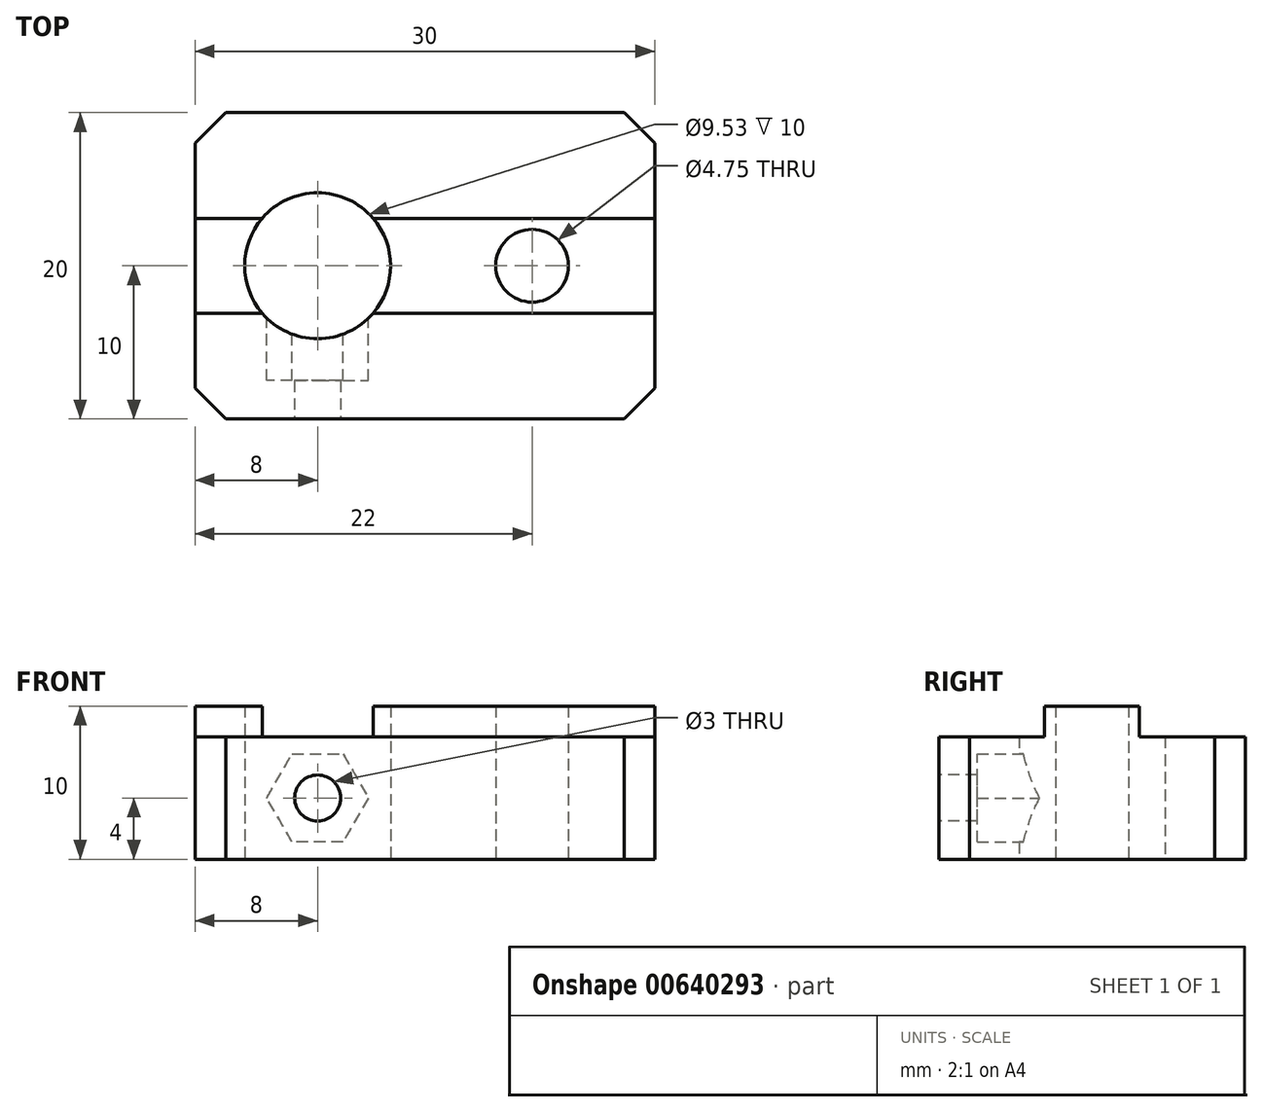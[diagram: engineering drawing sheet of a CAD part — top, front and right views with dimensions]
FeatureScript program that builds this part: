
annotation { "Feature Type Name" : "Feature", "Feature Type Description" : "" }
export const myFeature = defineFeature(function(context is Context, id is Id, definition is map)
    precondition{}
    {
        {
            var Q0;
            Q0=qCreatedBy(makeId("Top.planeOp"),FACE);
            var sketch = newSketch(context, id + "F0", { "sketchPlane" : qUnion([Q0])});
            skCircle(sketch, "E0", {"center": v(0, 0) * mm, "radius": 4.76 * mm});
            skLineSegment(sketch, "E1", {"start": v(0, 0) * mm, "end": v(0, 10) * mm, "construction": true});
            skLineSegment(sketch, "E2", {"start": v(0, 10) * mm, "end": v(-8, 10) * mm});
            skLineSegment(sketch, "E3", {"start": v(-8, 10) * mm, "end": v(-8, -10) * mm});
            skLineSegment(sketch, "E4", {"start": v(-8, -10) * mm, "end": v(22, -10) * mm});
            skLineSegment(sketch, "E5", {"start": v(22, -10) * mm, "end": v(22, 10) * mm});
            skLineSegment(sketch, "E6", {"start": v(22, 10) * mm, "end": v(0, 10) * mm});
            skLineSegment(sketch, "E7", {"start": v(22, 0) * mm, "end": v(14, 0) * mm, "construction": true});
            skPoint(sketch, "E7.endSnap0", {"position": v(22, 0) * mm});
            skCircle(sketch, "E8", {"center": v(14, 0) * mm, "radius": 2.38 * mm});
            skCircle(sketch, "E9", {"center": v(14, 0) * mm, "radius": 4.58 * mm, "construction": true});
            skSolve(sketch);
        }
        {
            var Q0;
            Q0 = qSketchRegion(id + "F0", true);
            extrude(context, id + "F1", {"entities" : qUnion([Q0]), "depth" : 8 * mm, "offsetDistance" : 25 * mm});
        }
        {
            var Q0;
            Q0=makeQuery(id+"F1.opExtrude","CAP_FACE",FACE,{"disambiguationData":[OSD([sQuery(id+"F0.wireOp",EDGE,"E0"),sQuery(id+"F0.wireOp",EDGE,"E2"),sQuery(id+"F0.wireOp",EDGE,"E3"),sQuery(id+"F0.wireOp",EDGE,"E4"),sQuery(id+"F0.wireOp",EDGE,"E5"),sQuery(id+"F0.wireOp",EDGE,"E6"),sQuery(id+"F0.wireOp",EDGE,"E8")])],"isStart":false});
            var sketch = newSketch(context, id + "F2", { "sketchPlane" : qUnion([Q0])});
            skLineSegment(sketch, "E10", {"start": v(0, 0) * mm, "end": v(0, 3.1) * mm, "construction": true});
            skLineSegment(sketch, "E11", {"start": v(0, 0) * mm, "end": v(0, -3.1) * mm, "construction": true});
            skLineSegment(sketch, "E12", {"start": v(22, 3.1) * mm, "end": v(3.62, 3.1) * mm});
            skLineSegment(sketch, "E13", {"start": v(-8, 3.1) * mm, "end": v(-8, -3.1) * mm});
            skLineSegment(sketch, "E14", {"start": v(-8, -3.1) * mm, "end": v(-3.62, -3.1) * mm});
            skLineSegment(sketch, "E15", {"start": v(22, -3.1) * mm, "end": v(22, 3.1) * mm});
            skArc(sketch, "E16.0", {"start": v(3.62, -3.1) * mm, "mid": v(4.76, 0) * mm, "end": v(3.62, 3.1) * mm});
            skCircle(sketch, "E16.1", {"center": v(14, 0) * mm, "radius": 2.37 * mm});
            skLineSegment(sketch, "E17.trimOffspring", {"start": v(-3.62, 3.1) * mm, "end": v(-8, 3.1) * mm});
            skLineSegment(sketch, "E18.trimOffspring", {"start": v(3.62, -3.1) * mm, "end": v(22, -3.1) * mm});
            skArc(sketch, "E19.trimOffspring", {"start": v(-3.62, 3.1) * mm, "mid": v(-4.76, 0) * mm, "end": v(-3.62, -3.1) * mm});
            skSolve(sketch);
        }
        {
            var Q0;
            Q0 = qSketchRegion(id + "F2", true);
            extrude(context, id + "F3", {"entities" : qUnion([Q0]), "operationType" : NewBodyOperationType.ADD, "depth" : 2 * mm, "offsetDistance" : 25 * mm});
        }
        {
            var Q0;
            Q0=makeQuery(id+"F1.opExtrude","SWEPT_FACE",FACE,{"disambiguationData":[OSD([sQuery(id+"F0.wireOp",EDGE,"E4")])]});
            var sketch = newSketch(context, id + "F4", { "sketchPlane" : qUnion([Q0])});
            skPoint(sketch, "E20.0", {"position": v(0, 0) * mm});
            skLineSegment(sketch, "E21", {"start": v(0, 0) * mm, "end": v(0, 8) * mm, "construction": true});
            skCircle(sketch, "E22", {"center": v(0, 4) * mm, "radius": 1.5 * mm});
            skSolve(sketch);
        }
        {
            var Q0;
            Q0 = qSketchRegion(id + "F4", true);
            extrude(context, id + "F5", {"entities" : qUnion([Q0]), "operationType" : NewBodyOperationType.REMOVE, "oppositeDirection" : true, "depth" : 10 * mm, "offsetDistance" : 25 * mm});
        }
        {
            var Q0;
            Q0=qCreatedBy(makeId("Front.planeOp"),FACE);
            var sketch = newSketch(context, id + "F6", { "sketchPlane" : qUnion([Q0])});
            skCircle(sketch, "E23.0", {"center": v(0, 4) * mm, "radius": 1.5 * mm, "construction": true});
            skCircle(sketch, "E24.cCircle", {"center": v(0, 4) * mm, "radius": 2.88 * mm, "construction": true});
            skLineSegment(sketch, "E24.0", {"start": v(1.66, 1.13) * mm, "end": v(-1.66, 1.13) * mm});
            skLineSegment(sketch, "E24.1", {"start": v(-1.66, 1.12) * mm, "end": v(-3.32, 4) * mm});
            skLineSegment(sketch, "E24.2", {"start": v(-3.32, 4) * mm, "end": v(-1.66, 6.88) * mm});
            skLineSegment(sketch, "E24.3", {"start": v(-1.66, 6.87) * mm, "end": v(1.66, 6.87) * mm});
            skLineSegment(sketch, "E24.4", {"start": v(1.66, 6.88) * mm, "end": v(3.32, 4) * mm});
            skLineSegment(sketch, "E24.5", {"start": v(3.32, 4) * mm, "end": v(1.66, 1.12) * mm});
            skPoint(sketch, "E24.0.midPoint", {"position": v(0, 1.13) * mm});
            skSolve(sketch);
        }
        {
            var Q0;
            Q0 = qSketchRegion(id + "F6", true);
            extrude(context, id + "F7", {"entities" : qUnion([Q0]), "operationType" : NewBodyOperationType.REMOVE, "depth" : 7.5 * mm, "offsetDistance" : 25 * mm});
        }
        {
            var Q0;
            Q0=makeQuery(id+"F1.opExtrude","SWEPT_EDGE",EDGE,{"disambiguationData":[OSD([sQuery(id+"F0.wireOp",EDGE,"E2"),sQuery(id+"F0.wireOp",EDGE,"E3")])]});
            var Q1;
            Q1=makeQuery(id+"F1.opExtrude","SWEPT_EDGE",EDGE,{"disambiguationData":[OSD([sQuery(id+"F0.wireOp",EDGE,"E5"),sQuery(id+"F0.wireOp",EDGE,"E6")])]});
            var Q2;
            Q2=makeQuery(id+"F1.opExtrude","SWEPT_EDGE",EDGE,{"disambiguationData":[OSD([sQuery(id+"F0.wireOp",EDGE,"E4"),sQuery(id+"F0.wireOp",EDGE,"E5")])]});
            var Q3;
            Q3=makeQuery(id+"F1.opExtrude","SWEPT_EDGE",EDGE,{"disambiguationData":[OSD([sQuery(id+"F0.wireOp",EDGE,"E3"),sQuery(id+"F0.wireOp",EDGE,"E4")])]});
            chamfer(context, id + "F8", {"entities" : qUnion([Q0, Q1, Q2, Q3]), "width" : 2 * mm, "tangentPropagation" : true});
        }
    });
